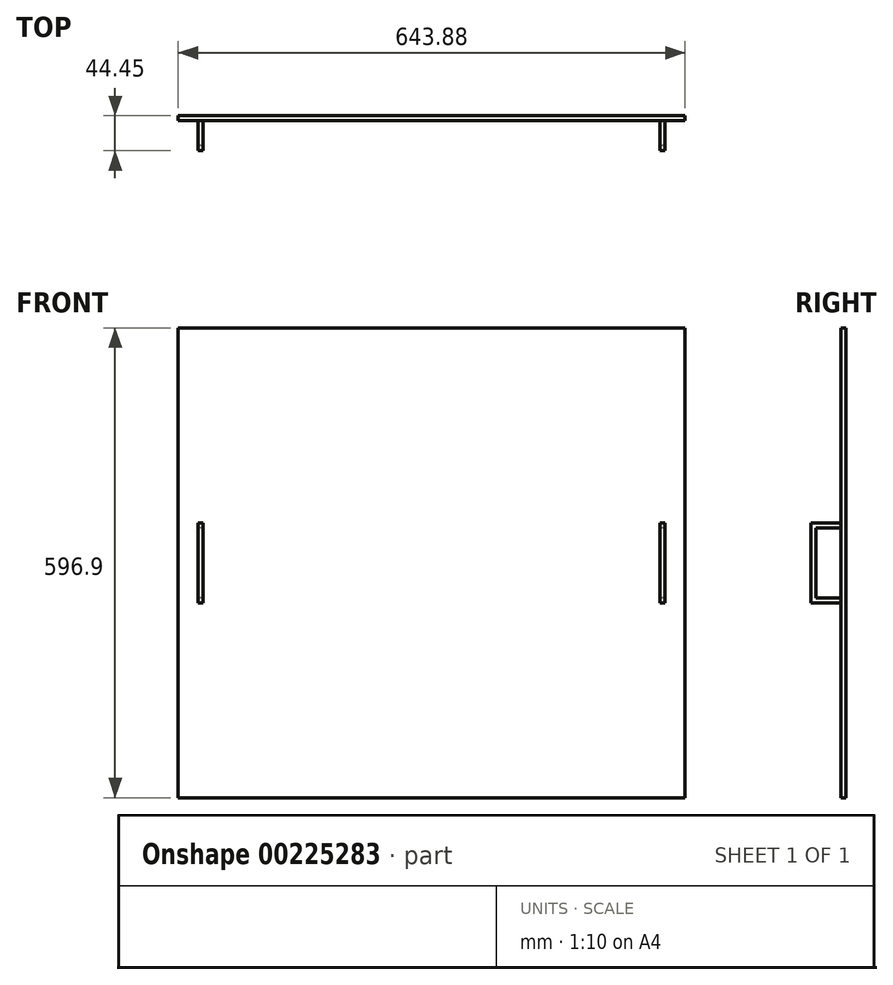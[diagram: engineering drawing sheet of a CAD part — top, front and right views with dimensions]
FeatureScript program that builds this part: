
annotation { "Feature Type Name" : "Feature", "Feature Type Description" : "" }
export const myFeature = defineFeature(function(context is Context, id is Id, definition is map)
    precondition{}
    {
        {
            var Q0;
            Q0=qCreatedBy(makeId("Front.planeOp"),FACE);
            var sketch = newSketch(context, id + "F0", { "sketchPlane" : qUnion([Q0])});
            skLineSegment(sketch, "E0.bottom", {"start": v(321.95, 298.45) * mm, "end": v(-321.95, 298.45) * mm});
            skLineSegment(sketch, "E0.top", {"start": v(321.95, -298.45) * mm, "end": v(-321.95, -298.45) * mm});
            skLineSegment(sketch, "E0.left", {"start": v(321.95, 298.45) * mm, "end": v(321.95, -298.45) * mm});
            skLineSegment(sketch, "E0.right", {"start": v(-321.95, 298.45) * mm, "end": v(-321.95, -298.45) * mm});
            skPoint(sketch, "E0.middle", {"position": v(0, 0) * mm});
            skSolve(sketch);
        }
        {
            var Q0;
            Q0=makeQuery(id+"F0.imprint","IMPRINT",FACE,{"disambiguationData":[TD([[makeQuery(id+"F0.imprint","IMPRINT",EDGE,{"derivedFrom":sQuery(id+"F0.wireOp",EDGE,"E0.bottom")}),1.0]])]});
            extrude(context, id + "F1", {"entities" : qUnion([Q0]), "depth" : 6.35 * mm});
        }
        {
            var Q0;
            Q0=makeQuery(id+"F1.opExtrude","CAP_FACE",FACE,{"disambiguationData":[OSD([sQuery(id+"F0.wireOp",EDGE,"E0.bottom"),sQuery(id+"F0.wireOp",EDGE,"E0.top"),sQuery(id+"F0.wireOp",EDGE,"E0.left"),sQuery(id+"F0.wireOp",EDGE,"E0.right")])],"isStart":false});
            var sketch = newSketch(context, id + "F2", { "sketchPlane" : qUnion([Q0])});
            skLineSegment(sketch, "E1.bottom", {"start": v(296.55, 50.8) * mm, "end": v(290.2, 50.8) * mm});
            skLineSegment(sketch, "E1.top", {"start": v(296.55, -50.8) * mm, "end": v(290.2, -50.8) * mm});
            skLineSegment(sketch, "E1.left", {"start": v(296.55, 50.8) * mm, "end": v(296.55, -50.8) * mm});
            skLineSegment(sketch, "E1.right", {"start": v(290.2, 50.8) * mm, "end": v(290.2, -50.8) * mm});
            skLineSegment(sketch, "E2", {"start": v(0, 413.02) * mm, "end": v(0, -407.73) * mm, "construction": true});
            skPoint(sketch, "E2.endSnap0", {"position": v(0, -298.45) * mm});
            skLineSegment(sketch, "E3.MirrorCS", {"start": v(-290.2, 50.8) * mm, "end": v(-290.2, -50.8) * mm});
            skLineSegment(sketch, "E4.MirrorCS", {"start": v(-296.54, 50.8) * mm, "end": v(-296.54, -50.8) * mm});
            skLineSegment(sketch, "E5.MirrorCS", {"start": v(-296.54, -50.8) * mm, "end": v(-290.2, -50.8) * mm});
            skLineSegment(sketch, "E6.MirrorCS", {"start": v(-296.54, 50.8) * mm, "end": v(-290.2, 50.8) * mm});
            skSolve(sketch);
        }
        {
            var Q0;
            Q0=makeQuery(id+"F2.imprint","IMPRINT",FACE,{"disambiguationData":[TD([[makeQuery(id+"F2.imprint","IMPRINT",EDGE,{"derivedFrom":sQuery(id+"F2.wireOp",EDGE,"E3.MirrorCS")}),-1.0]])]});
            var Q1;
            Q1=makeQuery(id+"F2.imprint","IMPRINT",FACE,{"disambiguationData":[TD([[makeQuery(id+"F2.imprint","IMPRINT",EDGE,{"derivedFrom":sQuery(id+"F2.wireOp",EDGE,"E1.bottom")}),1.0]])]});
            extrude(context, id + "F3", {"entities" : qUnion([Q0, Q1]), "operationType" : NewBodyOperationType.ADD, "depth" : 38.1 * mm});
        }
        {
            var Q0;
            Q0=makeQuery(id+"F3.opExtrude","SWEPT_FACE",FACE,{"disambiguationData":[OSD([sQuery(id+"F2.wireOp",EDGE,"E4.MirrorCS")])]});
            var sketch = newSketch(context, id + "F4", { "sketchPlane" : qUnion([Q0])});
            skLineSegment(sketch, "E7.0", {"start": v(6.35, 298.45) * mm, "end": v(6.35, -298.45) * mm});
            skLineSegment(sketch, "E8.0", {"start": v(44.45, 50.8) * mm, "end": v(44.45, -50.8) * mm});
            skLineSegment(sketch, "E9.0", {"start": v(44.45, 50.8) * mm, "end": v(6.35, 50.8) * mm});
            skLineSegment(sketch, "E10.bottom", {"start": v(38.1, -44.45) * mm, "end": v(6.35, -44.45) * mm});
            skLineSegment(sketch, "E10.top", {"start": v(38.1, 44.45) * mm, "end": v(6.35, 44.45) * mm});
            skLineSegment(sketch, "E10.left", {"start": v(38.1, -44.45) * mm, "end": v(38.1, 44.45) * mm});
            skLineSegment(sketch, "E10.right", {"start": v(6.35, -44.45) * mm, "end": v(6.35, 44.45) * mm});
            skSolve(sketch);
        }
        {
            var Q0;
            Q0=makeQuery(id+"F4.imprint","IMPRINT",FACE,{"disambiguationData":[TD([[makeQuery(id+"F4.imprint","IMPRINT",EDGE,{"derivedFrom":sQuery(id+"F4.wireOp",EDGE,"E10.bottom")}),-1.0]])]});
            extrude(context, id + "F5", {"entities" : qUnion([Q0]), "operationType" : NewBodyOperationType.REMOVE, "oppositeDirection" : true, "depth" : 609.6 * mm});
        }
    });
